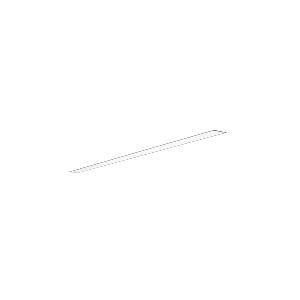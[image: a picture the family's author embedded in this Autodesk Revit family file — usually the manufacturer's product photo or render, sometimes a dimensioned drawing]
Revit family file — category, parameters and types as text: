
# Revit family: dotoo_line_-_dle_1000_840_d_00808222_4808
name_source: partatom
category: Lighting Fixtures
units: mm (PartAtom-declared; Revit-internal decimal feet)

## family parameters
Cut with Voids When Loaded = No
Host = Face
Light Source = No
Part Type = Normal
Room Calculation Point = No
Round Connector Dimension = Use Diameter
Shared = No

## types (1)
- DOTOO.line - DLE 1000/840/D (1 x LED, 1000 lm, 4000K)
    Apparent Load = 10 VA
    Approval mark = CE
    CIE Flux Codes = 67 91 98 100 100
    Color Rendering = 80-89
    Color Temperature = 4000K
    Control Gear = Electronic ballast
    Default Elevation = 1800 mm
    Description = DLE 1000/840/D|Recessed luminaire|light source:  |work equipment: Adjustable electronic ballast, digital DALI|connected load: 220-240 V, 50/60 Hz|Power consumption: approx. 9,5 W|standby: approx. 0,20|power factor: approx. 0,970|luminous flux: 1000 lm|luminous efficacy: 105 lm/W|light distribution: Direct|direct ratio: approx. 100 %|colour temperature: Cold white, ca. 4000 K|color rendering index (CRI): >= 80|chromaticity tolerance:  3 SDCM|System of protection: IP 40|class of protection: I|technology: Continuously dimmable|operation: External|luminaire body|material: Sectional aluminium|colour: White|lamp cover: Acrylic (PMMA), Clear|weight (net): approx. 3.1 kg|mains lead: Connector|Fastening: Fastening bow|glare control: Prism aperture|luminance(L65): <= 3000 cd/m|unified glare rating(4H 8H): <=  19|special features: DALI Load 1x, TouchDIM - dimming via standard switch, Flicker-free, Suitable as emergency lighting|
    Frequency = 50 Hz
    Height = 0 mm  [stored 0 ft]
    Lamp = 1 x LED
    Lamp Light Flux = 1000 lm
    Lamp count = 1
    Length = 854 mm
    Luminous efficacy = 105 lm/W
    Manufacturer = Waldmann
    ModVariant = No
    Model = 00808222
    Mounting Place = Ceiling
    Mounting Type = Recessed
    Number of Poles = 1
    OnlyDefault = Yes
    Power Factor = 1
    Product Name = DOTOO.line - DLE 1000/840/D
    Product group = Recessed luminaire
    ProductGroupID = 4
    Protection Class = Protection class I
    Protection Degree = IP 40
    RLX_Detail_Level = 1
    RLX_Emergency_Light_Flux = 0 lm
    RLX_Emergency_Type = 0
    RLX_Emergency_Type_DB = No
    RlxData = <blob elided: 12697 chars, md5=e78a5b11>
    Socket = socket
    Standby Power = 0 W
    System Light Flux = 1000 lm
    System Power = 10 W
    Type Comments = Product without accessories
    Type Image = 114404000-00808222.jpg
    URL = http://relux.com
    VarID = ---
    Voltage = 230 V
    Voltage Range = 220-240 V
    Weight = 0.00 kg
    Width = 60 mm  [stored 0.19685 ft]

note: [stored X ft] marks values corroborated as IEEE doubles in the binary element streams (Revit-internal decimal feet)

## geometry (parser evidence)
native form markers: Sweep x8
no freeform markers — native parametric forms only
